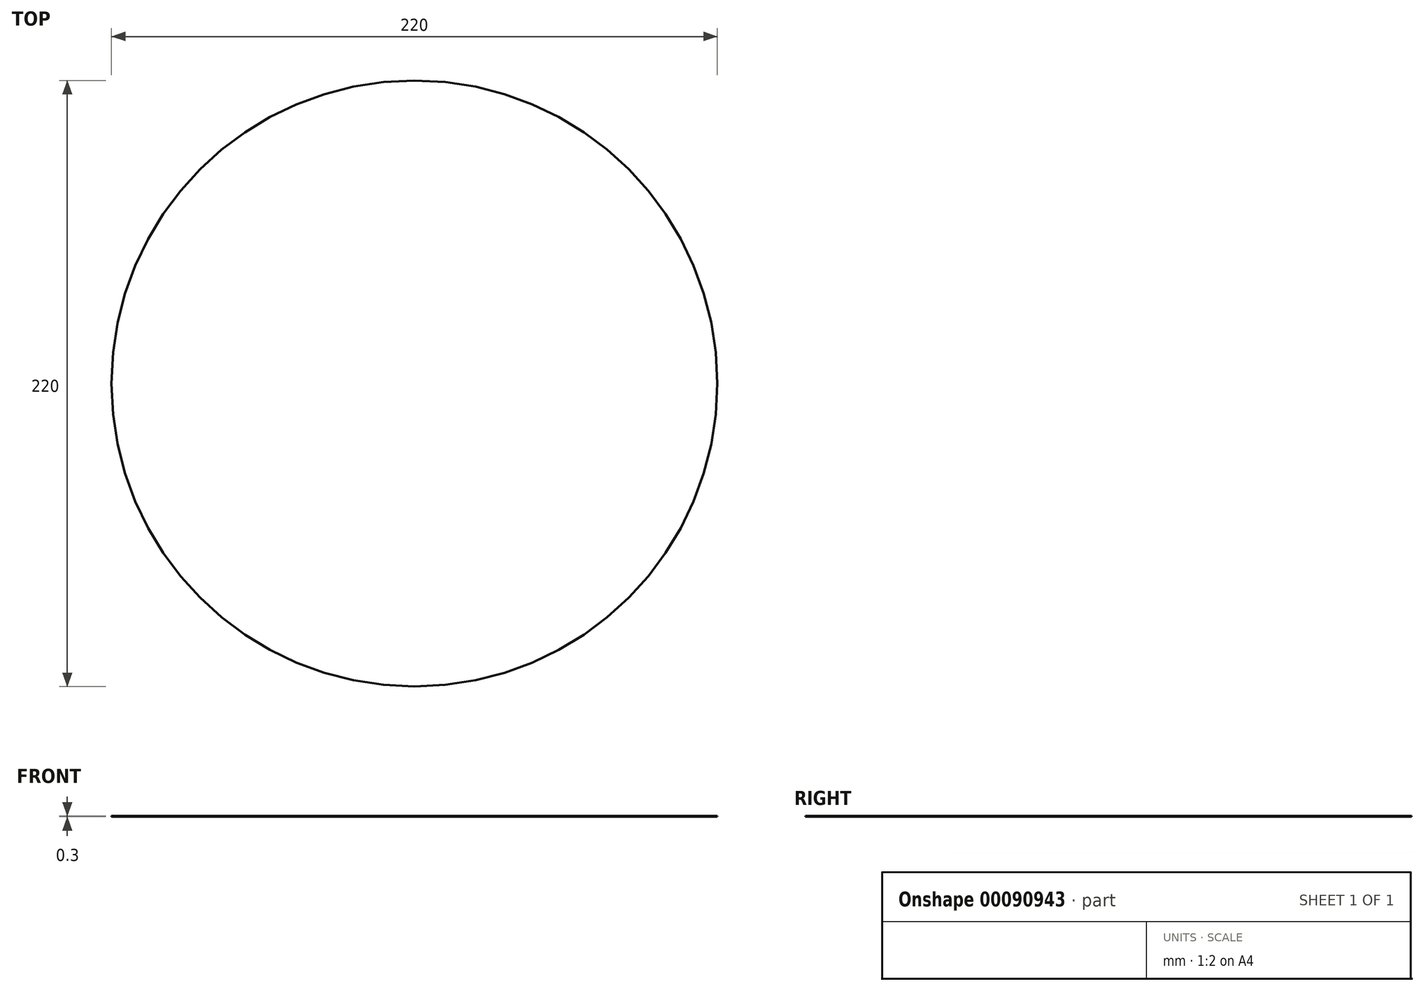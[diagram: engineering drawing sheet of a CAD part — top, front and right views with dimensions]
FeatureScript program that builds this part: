
annotation { "Feature Type Name" : "Feature", "Feature Type Description" : "" }
export const myFeature = defineFeature(function(context is Context, id is Id, definition is map)
    precondition{}
    {
        {
            var Q0;
            Q0=qCreatedBy(makeId("Top.planeOp"),FACE);
            var sketch = newSketch(context, id + "F0", { "sketchPlane" : qUnion([Q0])});
            skCircle(sketch, "E0", {"center": v(0, 0) * mm, "radius": 110 * mm});
            skSolve(sketch);
        }
        {
            var Q0;
            Q0 = qSketchRegion(id + "F0", true);
            extrude(context, id + "F1", {"entities" : qUnion([Q0]), "depth" : 0.3 * mm});
        }
    });
